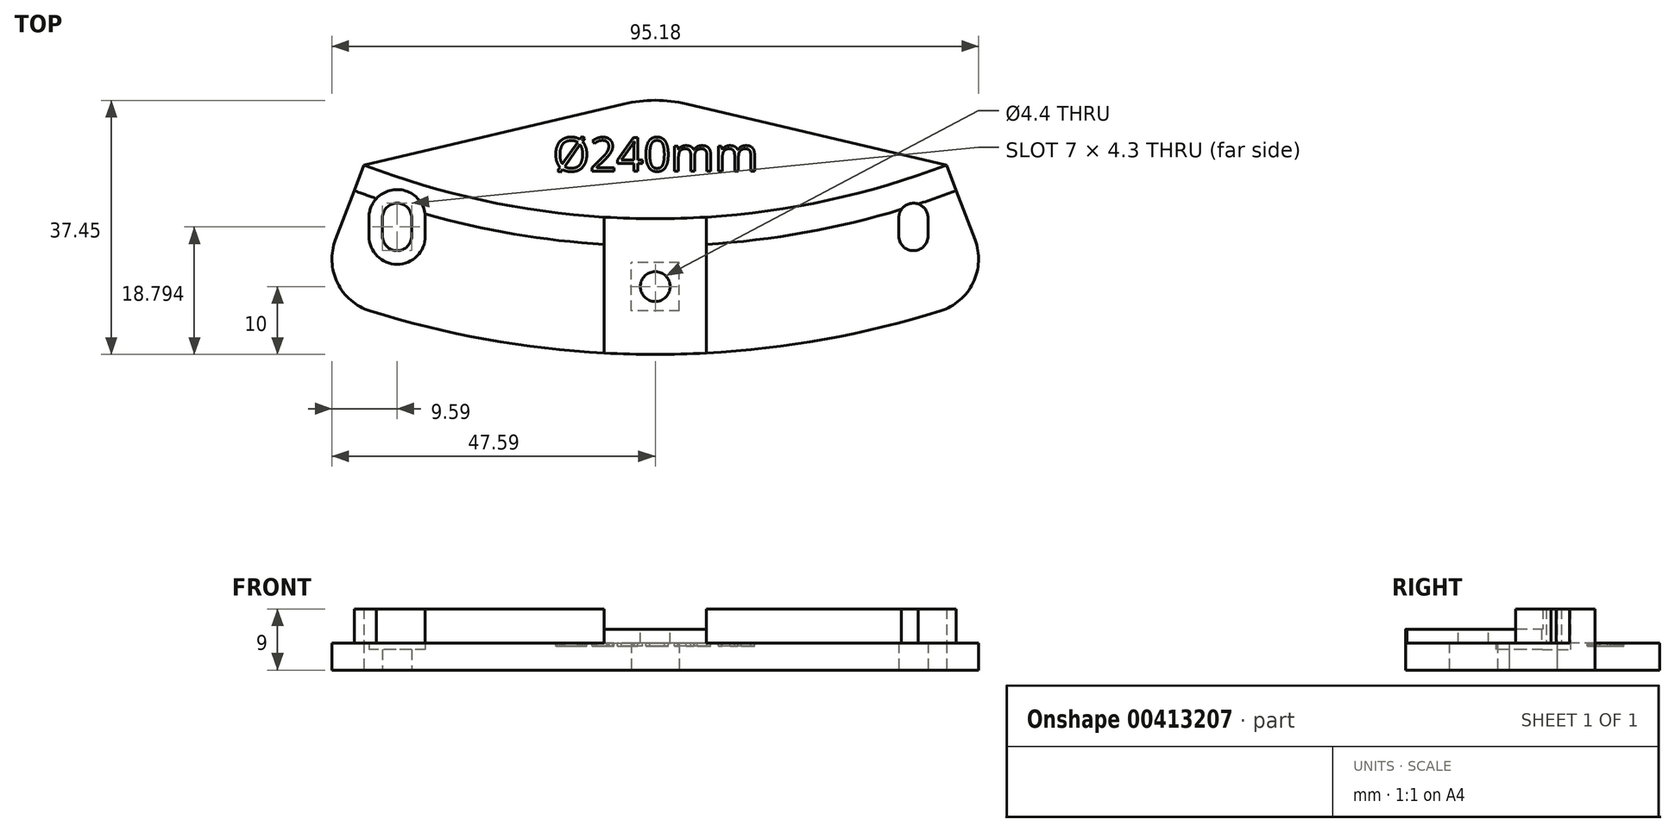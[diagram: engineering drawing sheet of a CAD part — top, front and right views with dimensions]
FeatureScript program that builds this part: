
annotation { "Feature Type Name" : "Feature", "Feature Type Description" : "" }
export const myFeature = defineFeature(function(context is Context, id is Id, definition is map)
    precondition{}
    {
        {
            var Q0;
            Q0=qCreatedBy(makeId("Top.planeOp"),FACE);
            var sketch = newSketch(context, id + "F0", { "sketchPlane" : qUnion([Q0])});
            skCircle(sketch, "E0", {"center": v(0, 0) * mm, "radius": 120.5 * mm});
            skSolve(sketch);
        }
        {
            var Q0;
            Q0=makeQuery(id+"F0.imprint","IMPRINT",FACE,{"disambiguationData":[TD([[makeQuery(id+"F0.imprint","IMPRINT",EDGE,{"derivedFrom":sQuery(id+"F0.wireOp",EDGE,"E0")}),1.0]])]});
            var sketch = newSketch(context, id + "F1", { "sketchPlane" : qUnion([Q0])});
            skArc(sketch, "E1.0", {"start": v(-42.88, -112.61) * mm, "mid": v(0, -120.5) * mm, "end": v(42.88, -112.61) * mm});
            skLineSegment(sketch, "E2", {"start": v(0, 0) * mm, "end": v(0, -120.5) * mm, "construction": true});
            skArc(sketch, "E3", {"start": v(-50, -131.3) * mm, "mid": v(0, -140.5) * mm, "end": v(50, -131.3) * mm});
            skLineSegment(sketch, "E4", {"start": v(-42.88, -112.61) * mm, "end": v(-50, -131.3) * mm});
            skLineSegment(sketch, "E5.MirrorCS", {"start": v(42.88, -112.61) * mm, "end": v(50, -131.3) * mm});
            skLineSegment(sketch, "E6", {"start": v(-42.88, -112.61) * mm, "end": v(0, -102.5) * mm});
            skLineSegment(sketch, "E7", {"start": v(0, -102.5) * mm, "end": v(42.88, -112.61) * mm});
            skArc(sketch, "E8", {"start": v(-44.3, -116.35) * mm, "mid": v(0, -124.5) * mm, "end": v(44.3, -116.35) * mm});
            skLineSegment(sketch, "E9", {"start": v(0, -120.5) * mm, "end": v(0, -140.5) * mm, "construction": true});
            skLineSegment(sketch, "E10", {"start": v(-7.5, -120.27) * mm, "end": v(-7.5, -140.3) * mm});
            skLineSegment(sketch, "E11.MirrorCS", {"start": v(7.5, -120.27) * mm, "end": v(7.5, -140.3) * mm});
            skSolve(sketch);
        }
        {
            var Q0;
            Q0=makeQuery(id+"F0.imprint","IMPRINT",FACE,{"disambiguationData":[TD([[makeQuery(id+"F0.imprint","IMPRINT",EDGE,{"derivedFrom":sQuery(id+"F0.wireOp",EDGE,"E0")}),1.0]])]});
            var sketch = newSketch(context, id + "F2", { "sketchPlane" : qUnion([Q0])});
            skPoint(sketch, "E12.0", {"position": v(0, -130.5) * mm});
            skLineSegment(sketch, "E13.bottom", {"start": v(3.55, -134.05) * mm, "end": v(-3.55, -134.05) * mm});
            skLineSegment(sketch, "E13.top", {"start": v(3.55, -126.95) * mm, "end": v(-3.55, -126.95) * mm});
            skLineSegment(sketch, "E13.left", {"start": v(3.55, -134.05) * mm, "end": v(3.55, -126.95) * mm});
            skLineSegment(sketch, "E13.right", {"start": v(-3.55, -134.05) * mm, "end": v(-3.55, -126.95) * mm});
            skSolve(sketch);
        }
        {
            var Q0;
            Q0=qCreatedBy(makeId("Top.planeOp"),FACE);
            var sketch = newSketch(context, id + "F3", { "sketchPlane" : qUnion([Q0])});
            skCircle(sketch, "E14", {"center": v(0, 0) * mm, "radius": 100.5 * mm});
            skCircle(sketch, "E15.cCircle", {"center": v(0, 0) * mm, "radius": 106 * mm, "construction": true});
            skLineSegment(sketch, "E15.0", {"start": v(183.6, -106) * mm, "end": v(-183.6, -106) * mm, "construction": true});
            skLineSegment(sketch, "E15.1", {"start": v(-183.6, -106) * mm, "end": v(0, 212) * mm, "construction": true});
            skLineSegment(sketch, "E15.2", {"start": v(0, 212) * mm, "end": v(183.6, -106) * mm, "construction": true});
            skPoint(sketch, "E15.0.midPoint", {"position": v(0, -106) * mm});
            skCircle(sketch, "E16", {"center": v(0, 0) * mm, "radius": 115 * mm});
            skPoint(sketch, "E17", {"position": v(0, -100.5) * mm});
            skLineSegment(sketch, "E18.MirrorCS", {"start": v(172.05, -86) * mm, "end": v(-172.05, -86) * mm, "construction": true});
            skLineSegment(sketch, "E19", {"start": v(0, 0) * mm, "end": v(-52, -86) * mm, "construction": true});
            skLineSegment(sketch, "E20", {"start": v(-52, -86) * mm, "end": v(-59.5, -98.4) * mm});
            skCircle(sketch, "E21", {"center": v(0, 0) * mm, "radius": 104.5 * mm});
            skLineSegment(sketch, "E22", {"start": v(-52, -86) * mm, "end": v(0, -82.5) * mm});
            skLineSegment(sketch, "E23.MirrorCS", {"start": v(0, 0) * mm, "end": v(52, -86) * mm, "construction": true});
            skLineSegment(sketch, "E24.MirrorCS", {"start": v(52, -86) * mm, "end": v(59.5, -98.4) * mm});
            skLineSegment(sketch, "E25.MirrorCS", {"start": v(52, -86) * mm, "end": v(0, -82.5) * mm});
            skLineSegment(sketch, "E26", {"start": v(0, -106) * mm, "end": v(0, -115) * mm});
            skLineSegment(sketch, "E27", {"start": v(-7.5, -114.76) * mm, "end": v(-7.5, -100.22) * mm});
            skLineSegment(sketch, "E28.MirrorCS", {"start": v(7.5, -114.76) * mm, "end": v(7.5, -100.22) * mm});
            skSolve(sketch);
        }
        {
            var Q0;
            Q0=makeQuery(id+"F1.imprint","IMPRINT",FACE,{"disambiguationData":[TD([[makeQuery(id+"F1.imprint","IMPRINT",EDGE,{"derivedFrom":sQuery(id+"F1.wireOp",EDGE,"E1.0")}),1.0]])]});
            extrude(context, id + "F4", {"entities" : qUnion([Q0]), "offsetDistance" : 25 * mm, "depth" : 4 * mm});
        }
        {
            var Q0;
            {var subQ0=sQuery(id+"F1.wireOp",EDGE,"E4");var subQ5=sQuery(id+"F1.wireOp",EDGE,"E8");var subQ7=makeQuery(id+"F1.imprint","INTERSECT",VERTEX,{"derivedFrom":[subQ0,subQ5]});Q0=makeQuery(id+"F1.imprint","IMPRINT",FACE,{"disambiguationData":[TD([[makeQuery(id+"F1.imprint","IMPRINT",EDGE,{"disambiguationData":[TD([[subQ7,-1.0]])],"derivedFrom":subQ5}),1.0]])]});}
            var Q1;
            {var subQ0=sQuery(id+"F1.wireOp",EDGE,"E5.MirrorCS");var subQ5=sQuery(id+"F1.wireOp",EDGE,"E8");var subQ7=makeQuery(id+"F1.imprint","INTERSECT",VERTEX,{"derivedFrom":[subQ0,subQ5]});Q1=makeQuery(id+"F1.imprint","IMPRINT",FACE,{"disambiguationData":[TD([[makeQuery(id+"F1.imprint","IMPRINT",EDGE,{"disambiguationData":[TD([[subQ7,1.0]])],"derivedFrom":subQ5}),1.0]])]});}
            extrude(context, id + "F5", {"entities" : qUnion([Q0, Q1]), "operationType" : NewBodyOperationType.ADD, "offsetDistance" : 25 * mm, "depth" : 9 * mm});
        }
        {
            var Q0;
            {var subQ0=sQuery(id+"F1.wireOp",EDGE,"E4");var subQ1=sQuery(id+"F1.wireOp",EDGE,"E3");var subQ2=makeQuery(id+"F1.imprint","INTERSECT",VERTEX,{"derivedFrom":[subQ1,subQ0]});Q0=makeQuery(id+"F1.imprint","IMPRINT",FACE,{"disambiguationData":[TD([[makeQuery(id+"F1.imprint","IMPRINT",EDGE,{"disambiguationData":[TD([[subQ2,-1.0]])],"derivedFrom":subQ1}),1.0]])]});}
            var Q1;
            {var subQ0=sQuery(id+"F1.wireOp",EDGE,"E5.MirrorCS");var subQ1=sQuery(id+"F1.wireOp",EDGE,"E3");var subQ2=makeQuery(id+"F1.imprint","INTERSECT",VERTEX,{"derivedFrom":[subQ1,subQ0]});Q1=makeQuery(id+"F1.imprint","IMPRINT",FACE,{"disambiguationData":[TD([[makeQuery(id+"F1.imprint","IMPRINT",EDGE,{"disambiguationData":[TD([[subQ2,1.0]])],"derivedFrom":subQ1}),1.0]])]});}
            extrude(context, id + "F6", {"entities" : qUnion([Q0, Q1]), "operationType" : NewBodyOperationType.ADD, "offsetDistance" : 25 * mm, "depth" : 4 * mm});
        }
        {
            var Q0;
            {var subQ0=sQuery(id+"F1.wireOp",EDGE,"E10");var subQ1=sQuery(id+"F1.wireOp",EDGE,"E1.0");var subQ2=makeQuery(id+"F1.imprint","INTERSECT",VERTEX,{"derivedFrom":[subQ1,subQ0]});Q0=makeQuery(id+"F1.imprint","IMPRINT",FACE,{"disambiguationData":[TD([[makeQuery(id+"F1.imprint","IMPRINT",EDGE,{"disambiguationData":[TD([[subQ2,-1.0]])],"derivedFrom":subQ1}),-1.0]])]});}
            var Q1;
            {var subQ0=sQuery(id+"F1.wireOp",EDGE,"E10");var subQ1=sQuery(id+"F1.wireOp",EDGE,"E3");var subQ2=makeQuery(id+"F1.imprint","INTERSECT",VERTEX,{"derivedFrom":[subQ1,subQ0]});Q1=makeQuery(id+"F1.imprint","IMPRINT",FACE,{"disambiguationData":[TD([[makeQuery(id+"F1.imprint","IMPRINT",EDGE,{"disambiguationData":[TD([[subQ2,-1.0]])],"derivedFrom":subQ1}),1.0]])]});}
            extrude(context, id + "F7", {"entities" : qUnion([Q0, Q1]), "operationType" : NewBodyOperationType.ADD, "offsetDistance" : 25 * mm, "depth" : 6 * mm});
        }
        {
            var Q0;
            Q0=makeQuery(id+"F6.opExtrude","SWEPT_EDGE",EDGE,{"disambiguationData":[OSD([sQuery(id+"F1.wireOp",EDGE,"E3"),sQuery(id+"F1.wireOp",EDGE,"E4")])]});
            var Q1;
            Q1=makeQuery(id+"F6.opExtrude","SWEPT_EDGE",EDGE,{"disambiguationData":[OSD([sQuery(id+"F1.wireOp",EDGE,"E3"),sQuery(id+"F1.wireOp",EDGE,"E5.MirrorCS")])]});
            fillet(context, id + "F8", {"entities" : qUnion([Q0, Q1]), "radius" : 8 * mm, "tangentPropagation" : true, "allowEdgeOverflow" : false});
        }
        {
            var Q0;
            Q0=makeQuery(id+"F4.opExtrude","SWEPT_EDGE",EDGE,{"disambiguationData":[OSD([sQuery(id+"F1.wireOp",EDGE,"E6"),sQuery(id+"F1.wireOp",EDGE,"E7")])]});
            fillet(context, id + "F9", {"entities" : qUnion([Q0]), "radius" : 20 * mm, "tangentPropagation" : true, "allowEdgeOverflow" : false});
        }
        {
            var Q0;
            Q0=makeQuery(id+"F2.imprint","IMPRINT",FACE,{"disambiguationData":[TD([[makeQuery(id+"F2.imprint","IMPRINT",EDGE,{"derivedFrom":sQuery(id+"F2.wireOp",EDGE,"E13.bottom")}),-1.0]])]});
            extrude(context, id + "F10", {"entities" : qUnion([Q0]), "operationType" : NewBodyOperationType.REMOVE, "offsetDistance" : 25 * mm, "depth" : 4 * mm});
        }
        {
            var Q0;
            Q0=sQuery(id+"F2.wireOp",VERTEX,"E12.0");
            var Q1;
            Q1=makeQuery(id+"F4.opExtrude","SWEPT_BODY",BODY,{"disambiguationData":[OSD([sQuery(id+"F1.wireOp",EDGE,"E1.0"),sQuery(id+"F1.wireOp",EDGE,"E6"),sQuery(id+"F1.wireOp",EDGE,"E7")])]});
            hole(context, id + "F11", {"style" : HoleStyle.SIMPLE, "endStyle" : HoleEndStyle.THROUGH, "oppositeDirection" : true, "holeDiameter" : 4.4 * mm, "majorDiameter" : 5 * mm, "isTappedThrough" : true, "tappedDepth" : 12 * mm, "tapClearance" : 3, "locations" : qUnion([Q0]), "scope" : qUnion([Q1])});
        }
        {
            var Q0;
            Q0=qCreatedBy(makeId("Top.planeOp"),FACE);
            var sketch = newSketch(context, id + "F12", { "sketchPlane" : qUnion([Q0])});
            skCircle(sketch, "E29", {"center": v(0, 0) * mm, "radius": 127.5 * mm, "construction": true});
            skLineSegment(sketch, "E30.bottom", {"start": v(-38, -118.2) * mm, "end": v(-38, -118.2) * mm});
            skLineSegment(sketch, "E30.top", {"start": v(-38, -125.2) * mm, "end": v(-38, -125.2) * mm});
            skLineSegment(sketch, "E30.left", {"start": v(-35.85, -120.36) * mm, "end": v(-35.85, -123.06) * mm});
            skLineSegment(sketch, "E30.right", {"start": v(-40.15, -120.36) * mm, "end": v(-40.15, -123.06) * mm});
            skPoint(sketch, "E30.middle", {"position": v(-38, -121.7) * mm});
            skPoint(sketch, "E31.visualSharp", {"position": v(-35.85, -118.2) * mm});
            skArc(sketch, "E31.filletArc", {"start": v(-35.85, -120.36) * mm, "mid": v(-36.48, -118.84) * mm, "end": v(-38, -118.2) * mm});
            skPoint(sketch, "E32.visualSharp", {"position": v(-40.15, -118.2) * mm});
            skArc(sketch, "E32.filletArc", {"start": v(-38, -118.2) * mm, "mid": v(-39.52, -118.84) * mm, "end": v(-40.15, -120.36) * mm});
            skPoint(sketch, "E33.visualSharp", {"position": v(-40.15, -125.2) * mm});
            skArc(sketch, "E33.filletArc", {"start": v(-40.15, -123.06) * mm, "mid": v(-39.52, -124.58) * mm, "end": v(-38, -125.2) * mm});
            skPoint(sketch, "E34.visualSharp", {"position": v(-35.85, -125.2) * mm});
            skArc(sketch, "E34.filletArc", {"start": v(-38, -125.2) * mm, "mid": v(-36.48, -124.58) * mm, "end": v(-35.85, -123.06) * mm});
            skArc(sketch, "E35.0", {"start": v(-33.85, -120.36) * mm, "mid": v(-35.07, -117.42) * mm, "end": v(-38, -116.2) * mm});
            skArc(sketch, "E35.1", {"start": v(-38, -127.2) * mm, "mid": v(-35.07, -126) * mm, "end": v(-33.85, -123.06) * mm});
            skArc(sketch, "E35.2", {"start": v(-42.15, -123.06) * mm, "mid": v(-40.93, -126) * mm, "end": v(-38, -127.2) * mm});
            skLineSegment(sketch, "E35.3", {"start": v(-33.85, -120.36) * mm, "end": v(-33.85, -123.06) * mm});
            skLineSegment(sketch, "E35.4", {"start": v(-42.15, -120.36) * mm, "end": v(-42.15, -123.06) * mm});
            skArc(sketch, "E35.5", {"start": v(-38, -116.2) * mm, "mid": v(-40.93, -117.42) * mm, "end": v(-42.15, -120.36) * mm});
            skPoint(sketch, "E36.MirrorP", {"position": v(40.15, -125.2) * mm});
            skPoint(sketch, "E37.MirrorP", {"position": v(35.85, -118.2) * mm});
            skPoint(sketch, "E38.MirrorP", {"position": v(40.15, -118.2) * mm});
            skPoint(sketch, "E39.MirrorP", {"position": v(35.85, -125.2) * mm});
            skLineSegment(sketch, "E40.MirrorCS", {"start": v(38, -118.2) * mm, "end": v(38, -118.2) * mm});
            skArc(sketch, "E41.MirrorCS", {"start": v(38, -116.2) * mm, "mid": v(40.93, -117.42) * mm, "end": v(42.15, -120.36) * mm});
            skLineSegment(sketch, "E42.MirrorCS", {"start": v(42.15, -120.36) * mm, "end": v(42.15, -123.06) * mm});
            skLineSegment(sketch, "E43.MirrorCS", {"start": v(38, -125.2) * mm, "end": v(38, -125.2) * mm});
            skLineSegment(sketch, "E44.MirrorCS", {"start": v(35.85, -120.36) * mm, "end": v(35.85, -123.06) * mm});
            skArc(sketch, "E45.MirrorCS", {"start": v(33.85, -120.36) * mm, "mid": v(35.07, -117.42) * mm, "end": v(38, -116.2) * mm});
            skLineSegment(sketch, "E46.MirrorCS", {"start": v(33.85, -120.36) * mm, "end": v(33.85, -123.06) * mm});
            skArc(sketch, "E47.MirrorCS", {"start": v(38, -125.2) * mm, "mid": v(36.48, -124.58) * mm, "end": v(35.85, -123.06) * mm});
            skArc(sketch, "E48.MirrorCS", {"start": v(38, -118.2) * mm, "mid": v(39.52, -118.84) * mm, "end": v(40.15, -120.36) * mm});
            skLineSegment(sketch, "E49.MirrorCS", {"start": v(40.15, -120.36) * mm, "end": v(40.15, -123.06) * mm});
            skArc(sketch, "E50.MirrorCS", {"start": v(35.85, -120.36) * mm, "mid": v(36.48, -118.84) * mm, "end": v(38, -118.2) * mm});
            skPoint(sketch, "E51.MirrorP", {"position": v(38, -121.7) * mm});
            skArc(sketch, "E52.MirrorCS", {"start": v(40.15, -123.06) * mm, "mid": v(39.52, -124.58) * mm, "end": v(38, -125.2) * mm});
            skArc(sketch, "E53.MirrorCS", {"start": v(42.15, -123.06) * mm, "mid": v(40.93, -126) * mm, "end": v(38, -127.2) * mm});
            skArc(sketch, "E54.MirrorCS", {"start": v(38, -127.2) * mm, "mid": v(35.07, -126) * mm, "end": v(33.85, -123.06) * mm});
            skPoint(sketch, "E55.0", {"position": v(0, -130.5) * mm});
            skSolve(sketch);
        }
        {
            var Q0;
            Q0=makeQuery(id+"F12.imprint","IMPRINT",FACE,{"disambiguationData":[TD([[makeQuery(id+"F12.imprint","IMPRINT",EDGE,{"derivedFrom":sQuery(id+"F12.wireOp",EDGE,"E30.left")}),1.0]])]});
            var Q1;
            Q1=makeQuery(id+"F12.imprint","IMPRINT",FACE,{"disambiguationData":[TD([[makeQuery(id+"F12.imprint","IMPRINT",EDGE,{"derivedFrom":sQuery(id+"F12.wireOp",EDGE,"E30.left")}),-1.0]])]});
            var Q2;
            Q2=makeQuery(id+"F12.imprint","IMPRINT",FACE,{"disambiguationData":[TD([[makeQuery(id+"F12.imprint","IMPRINT",EDGE,{"derivedFrom":sQuery(id+"F12.wireOp",EDGE,"E41.MirrorCS")}),-1.0]])]});
            var Q3;
            Q3=makeQuery(id+"F12.imprint","IMPRINT",FACE,{"disambiguationData":[TD([[makeQuery(id+"F12.imprint","IMPRINT",EDGE,{"derivedFrom":sQuery(id+"F12.wireOp",EDGE,"E44.MirrorCS")}),1.0]])]});
            extrude(context, id + "F13", {"entities" : qUnion([Q0, Q1, Q2, Q3]), "operationType" : NewBodyOperationType.REMOVE, "offsetDistance" : 25 * mm, "depth" : 10 * mm});
        }
        {
            var Q0;
            Q0=makeQuery(id+"F12.imprint","IMPRINT",FACE,{"disambiguationData":[TD([[makeQuery(id+"F12.imprint","IMPRINT",EDGE,{"derivedFrom":sQuery(id+"F12.wireOp",EDGE,"E30.left")}),1.0]])]});
            var Q1;
            Q1=makeQuery(id+"F12.imprint","IMPRINT",FACE,{"disambiguationData":[TD([[makeQuery(id+"F12.imprint","IMPRINT",EDGE,{"derivedFrom":sQuery(id+"F12.wireOp",EDGE,"E41.MirrorCS")}),-1.0]])]});
            extrude(context, id + "F14", {"entities" : qUnion([Q0, Q1]), "operationType" : NewBodyOperationType.ADD, "offsetDistance" : 25 * mm, "depth" : 3 * mm});
        }
        {
            var Q0;
            Q0=makeQuery(id+"F4.opExtrude","CAP_FACE",FACE,{"disambiguationData":[OSD([sQuery(id+"F1.wireOp",EDGE,"E1.0"),sQuery(id+"F1.wireOp",EDGE,"E6"),sQuery(id+"F1.wireOp",EDGE,"E7")])],"isStart":false});
            var sketch = newSketch(context, id + "F15", { "sketchPlane" : qUnion([Q0])});
            skPoint(sketch, "E56.0", {"position": v(0, -102.5) * mm});
            skText(sketch, "E57", { "text": "Ø240mm", "fontName": "OpenSans-Regular.ttf"});
            const initialGuessF15  = {"E57": [-0.01506, -0.1135, 1, 0, 0.005]};
            skSetInitialGuess(sketch, initialGuessF15);
            skSolve(sketch);
        }
        {
            var Q0;
            Q0 = qSketchRegion(id + "F15", true);
            var Q1;
            Q1=makeQuery(id+"F4.opExtrude","CAP_FACE",FACE,{"disambiguationData":[OSD([sQuery(id+"F1.wireOp",EDGE,"E1.0"),sQuery(id+"F1.wireOp",EDGE,"E6"),sQuery(id+"F1.wireOp",EDGE,"E7")])],"isStart":false});
            var Q2;
            Q2=makeQuery(id+"F4.opExtrude","CAP_FACE",FACE,{"disambiguationData":[OSD([sQuery(id+"F1.wireOp",EDGE,"E1.0"),sQuery(id+"F1.wireOp",EDGE,"E6"),sQuery(id+"F1.wireOp",EDGE,"E7")])],"isStart":false});
            extrude(context, id + "F16", {"entities" : qUnion([Q0]), "operationType" : NewBodyOperationType.REMOVE, "oppositeDirection" : true, "endBoundEntityFace" : qUnion([Q1]), "offsetDistance" : 25 * mm, "depth" : .5 * mm, "hasSecondDirectionOffset" : true, "secondDirectionOffsetDistance" : 5 * mm, "secondDirectionOffsetOppositeDirection" : true});
        }
    });
